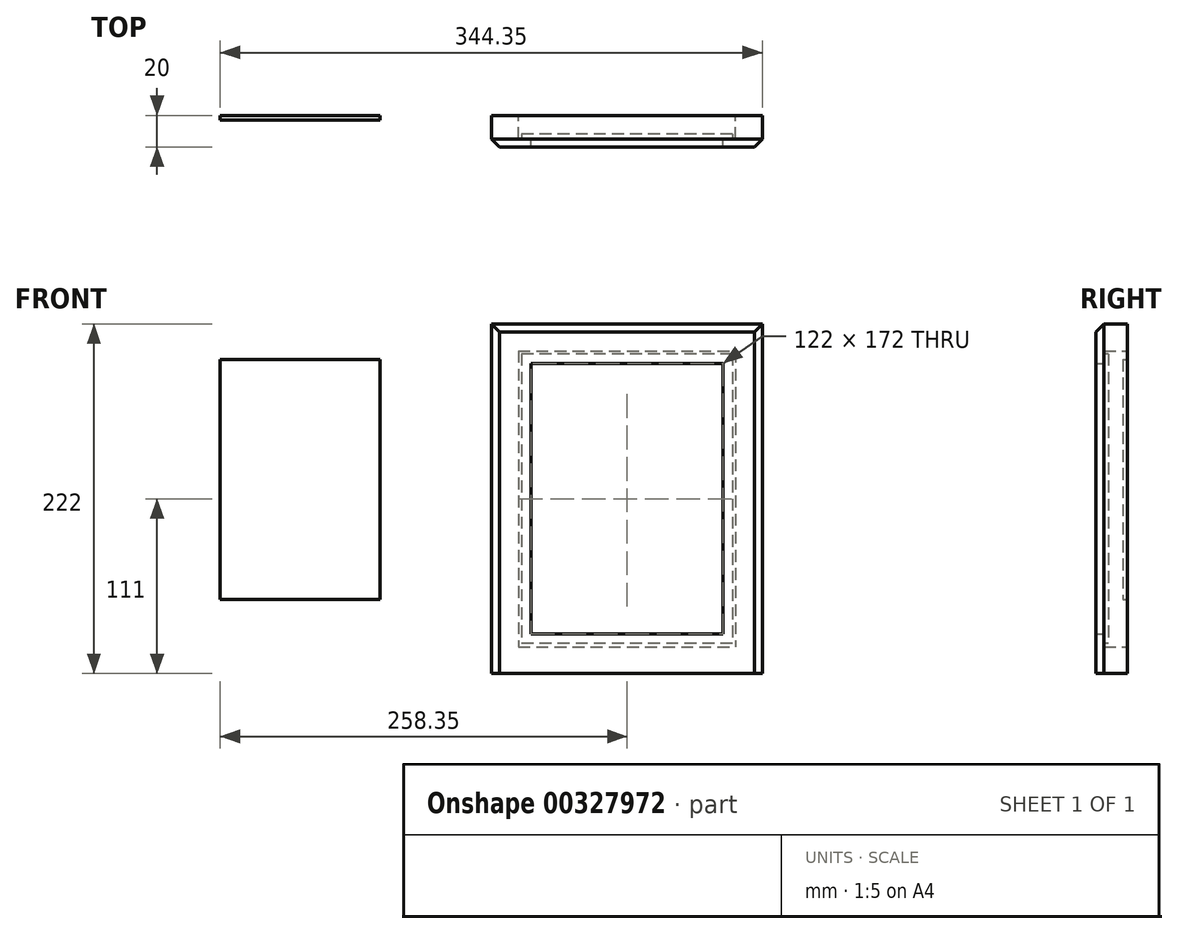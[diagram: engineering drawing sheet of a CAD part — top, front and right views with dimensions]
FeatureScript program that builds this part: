
annotation { "Feature Type Name" : "Feature", "Feature Type Description" : "" }
export const myFeature = defineFeature(function(context is Context, id is Id, definition is map)
    precondition{}
    {
        {
            var Q0;
            Q0=qCreatedBy(makeId("Front.planeOp"),FACE);
            var sketch = newSketch(context, id + "F0", { "sketchPlane" : qUnion([Q0])});
            skLineSegment(sketch, "E0.bottom", {"start": v(-61, 86) * mm, "end": v(61, 86) * mm});
            skLineSegment(sketch, "E0.top", {"start": v(-61, -86) * mm, "end": v(61, -86) * mm});
            skLineSegment(sketch, "E0.left", {"start": v(-61, 86) * mm, "end": v(-61, -86) * mm});
            skLineSegment(sketch, "E0.right", {"start": v(61, 86) * mm, "end": v(61, -86) * mm});
            skPoint(sketch, "E0.middle", {"position": v(0, 0) * mm});
            skLineSegment(sketch, "E1.bottom", {"start": v(86, -111) * mm, "end": v(-86, -111) * mm});
            skLineSegment(sketch, "E1.top", {"start": v(86, 111) * mm, "end": v(-86, 111) * mm});
            skLineSegment(sketch, "E1.left", {"start": v(86, -111) * mm, "end": v(86, 111) * mm});
            skLineSegment(sketch, "E1.right", {"start": v(-86, -111) * mm, "end": v(-86, 111) * mm});
            skLineSegment(sketch, "E2.bottom", {"start": v(-86, -111) * mm, "end": v(86, -111) * mm});
            skSolve(sketch);
        }
        {
            var Q0;
            Q0 = qSketchRegion(id + "F0", true);
            extrude(context, id + "F1", {"entities" : qUnion([Q0]), "depth" : 20 * mm});
        }
        {
            var Q0;
            Q0=makeQuery(id+"F1.opExtrude","CAP_FACE",FACE,{"disambiguationData":[OSD([sQuery(id+"F0.wireOp",EDGE,"E0.bottom"),sQuery(id+"F0.wireOp",EDGE,"E0.top"),sQuery(id+"F0.wireOp",EDGE,"E0.left"),sQuery(id+"F0.wireOp",EDGE,"E0.right"),sQuery(id+"F0.wireOp",EDGE,"E1.bottom"),sQuery(id+"F0.wireOp",EDGE,"E1.top"),sQuery(id+"F0.wireOp",EDGE,"E1.left"),sQuery(id+"F0.wireOp",EDGE,"E1.right")])],"isStart":true});
            var sketch = newSketch(context, id + "F2", { "sketchPlane" : qUnion([Q0])});
            skLineSegment(sketch, "E3.bottom", {"start": v(69, 94) * mm, "end": v(-69, 94) * mm});
            skLineSegment(sketch, "E3.top", {"start": v(69, -94) * mm, "end": v(-69, -94) * mm});
            skLineSegment(sketch, "E3.left", {"start": v(69, 94) * mm, "end": v(69, -94) * mm});
            skLineSegment(sketch, "E3.right", {"start": v(-69, 94) * mm, "end": v(-69, -94) * mm});
            skPoint(sketch, "E3.middle", {"position": v(0, 0) * mm});
            skSolve(sketch);
        }
        {
            var Q0;
            Q0=makeQuery(id+"F2.imprint","IMPRINT",FACE,{"disambiguationData":[TD([[makeQuery(id+"F2.imprint","IMPRINT",EDGE,{"derivedFrom":sQuery(id+"F2.wireOp",EDGE,"E3.bottom")}),1.0]])]});
            extrude(context, id + "F3", {"entities" : qUnion([Q0]), "operationType" : NewBodyOperationType.REMOVE, "oppositeDirection" : true, "depth" : 15 * mm, "offsetDistance" : 25 * mm});
        }
        {
            var Q0;
            Q0=makeQuery(id+"F1.opExtrude","CAP_EDGE",EDGE,{"disambiguationData":[OSD([sQuery(id+"F0.wireOp",EDGE,"E1.right")])],"isStart":false});
            var Q1;
            Q1=makeQuery(id+"F1.opExtrude","CAP_EDGE",EDGE,{"disambiguationData":[OSD([sQuery(id+"F0.wireOp",EDGE,"E1.top")])],"isStart":false});
            var Q2;
            Q2=makeQuery(id+"F1.opExtrude","CAP_EDGE",EDGE,{"disambiguationData":[OSD([sQuery(id+"F0.wireOp",EDGE,"E1.left"),sQuery(id+"F0.wireOp",EDGE,"E2.right")])],"isStart":false});
            var Q3;
            Q3=makeQuery(id+"F1.opExtrude","CAP_EDGE",EDGE,{"disambiguationData":[OSD([sQuery(id+"F0.wireOp",EDGE,"E2.bottom")])],"isStart":false});
            chamfer(context, id + "F4", {"entities" : qUnion([Q0, Q1, Q2, Q3]), "width" : 5 * mm, "tangentPropagation" : true});
        }
        {
            var Q0;
            Q0=qCreatedBy(makeId("Front.planeOp"),FACE);
            var sketch = newSketch(context, id + "F5", { "sketchPlane" : qUnion([Q0])});
            skLineSegment(sketch, "E4.bottom", {"start": v(-156.75, 88.45) * mm, "end": v(-258.35, 88.45) * mm});
            skLineSegment(sketch, "E4.top", {"start": v(-156.75, -63.95) * mm, "end": v(-258.35, -63.95) * mm});
            skLineSegment(sketch, "E4.left", {"start": v(-156.75, 88.45) * mm, "end": v(-156.75, -63.95) * mm});
            skLineSegment(sketch, "E4.right", {"start": v(-258.35, 88.45) * mm, "end": v(-258.35, -63.95) * mm});
            skLineSegment(sketch, "E5", {"start": v(-258.35, 88.45) * mm, "end": v(-156.75, -63.95) * mm, "construction": true});
            skLineSegment(sketch, "E6", {"start": v(-258.35, -63.95) * mm, "end": v(-156.75, 88.45) * mm, "construction": true});
            skPoint(sketch, "E7", {"position": v(-207.55, 12.25) * mm});
            skSolve(sketch);
        }
        {
            var Q0;
            Q0=makeQuery(id+"F5.imprint","IMPRINT",FACE,{"disambiguationData":[TD([[makeQuery(id+"F5.imprint","IMPRINT",EDGE,{"derivedFrom":sQuery(id+"F5.wireOp",EDGE,"E4.bottom")}),1.0]])]});
            extrude(context, id + "F6", {"entities" : qUnion([Q0]), "depth" : 3 * mm});
        }
        {
            var Q0;
            Q0=makeQuery(id+"F1.opExtrude","CAP_FACE",FACE,{"disambiguationData":[OSD([sQuery(id+"F0.wireOp",EDGE,"E0.bottom"),sQuery(id+"F0.wireOp",EDGE,"E0.top"),sQuery(id+"F0.wireOp",EDGE,"E0.left"),sQuery(id+"F0.wireOp",EDGE,"E0.right"),sQuery(id+"F0.wireOp",EDGE,"E1.top"),sQuery(id+"F0.wireOp",EDGE,"E1.left"),sQuery(id+"F0.wireOp",EDGE,"E1.right"),sQuery(id+"F0.wireOp",EDGE,"E2.top"),sQuery(id+"F0.wireOp",EDGE,"E2.left"),sQuery(id+"F0.wireOp",EDGE,"E2.right")])],"isStart":false});
            var sketch = newSketch(context, id + "F7", { "sketchPlane" : qUnion([Q0])});
            skLineSegment(sketch, "E8", {"start": v(-61, 86) * mm, "end": v(61, -86) * mm, "construction": true});
            skLineSegment(sketch, "E9", {"start": v(-61, -86) * mm, "end": v(61, 86) * mm, "construction": true});
            skPoint(sketch, "E10", {"position": v(0, 0) * mm});
            skSolve(sketch);
        }
        {
            var Q0;
            Q0=makeQuery(id+"F3.boolean.opBoolean","COPY",FACE,{"derivedFrom":makeQuery(id+"F3.opExtrude","CAP_FACE",FACE,{"disambiguationData":[OSD([sQuery(id+"F0.wireOp",EDGE,"E0.bottom"),sQuery(id+"F0.wireOp",EDGE,"E0.top"),sQuery(id+"F0.wireOp",EDGE,"E0.left"),sQuery(id+"F0.wireOp",EDGE,"E0.right"),sQuery(id+"F2.wireOp",EDGE,"E3.bottom"),sQuery(id+"F2.wireOp",EDGE,"E3.top"),sQuery(id+"F2.wireOp",EDGE,"E3.left"),sQuery(id+"F2.wireOp",EDGE,"E3.right")])],"isStart":false})});
            var sketch = newSketch(context, id + "F8", { "sketchPlane" : qUnion([Q0])});
            skLineSegment(sketch, "E11.bottom", {"start": v(-67, 92) * mm, "end": v(67, 92) * mm});
            skLineSegment(sketch, "E11.top", {"start": v(-67, -92) * mm, "end": v(67, -92) * mm});
            skLineSegment(sketch, "E11.left", {"start": v(-67, 92) * mm, "end": v(-67, -92) * mm});
            skLineSegment(sketch, "E11.right", {"start": v(67, 92) * mm, "end": v(67, -92) * mm});
            skSolve(sketch);
        }
        {
            var Q0;
            Q0 = qSketchRegion(id + "F8", true);
            extrude(context, id + "F9", {"entities" : qUnion([Q0]), "depth" : 3 * mm, "offsetDistance" : 25 * mm});
        }
    });
